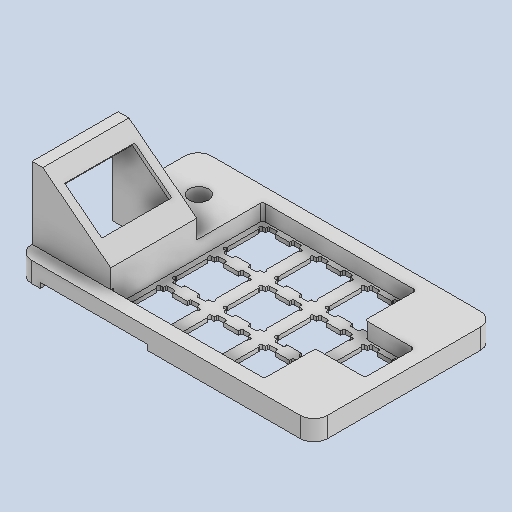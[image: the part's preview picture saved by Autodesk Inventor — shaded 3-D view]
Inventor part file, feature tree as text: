
AUTODESK INVENTOR PART (.ipt)
format: ipt  version: 2025.2 (Build 292293000, 293)  size: 1,165,312 bytes
history: native  units: mm
features: sketch x11, extrude x10, plane x2, fillet x2
ambient origin geometry x8: Origin, YZ Plane, XZ Plane, XY Plane, X Axis, Y Axis, Z Axis, Center Point
bodies: Solid1 (feature_tree)
feature tree (25):
  extrude  "Extrusion1"  Depth=19.0mm
  extrude  "Extrusion6"  Depth=1.5mm TaperAngle=0.0deg
  plane  "Work Plane3"
  sketch  "Sketch6"  dims[d41=2.0mm d43=6.0mm d44=0.0mm]
  extrude  "Extrusion7"  Depth=2.0mm
  extrude  "Extrusion8"  Depth=6.0mm TaperAngle=0.0deg
  sketch  "Sketch9"  dims[d51=32.0mm d52=7.0mm d53=0.0mm d54=32.0mm d55=4.0mm]
  plane  "Work Plane4"
  extrude  "Extrusion9"  Depth=31.0mm
  sketch  "Sketch10"  dims[d56=6.615149mm d57=7.0mm d58=0.0mm]
  extrude  "Extrusion10"  Depth=5.0mm
  extrude  "Extrusion11"  Depth=7.0mm TaperAngle=0.0deg
  fillet  "Fillet1"  Radius=32.0mm
  fillet  "Fillet2"  Radius=4.0mm
  extrude  "Extrusion12"  Depth=7.0mm TaperAngle=0.0deg
  extrude  "Extrusion13"  Depth=2.0mm
  extrude  "Extrusion14"  [1 undecoded]
  sketch  "Sketch1"  dims[d0=14.5mm d1=14.5mm d2=3.5mm d3=1.2mm d4=1.0mm d5=1.2mm d6=0.1mm d7=0.1mm d8=0.5mm d9=0.25mm d13=40.0mm d15=19.0mm d16=30.0mm d18=19.0mm d21=115.0mm]
  sketch  "Sketch Rectangular Pattern1"  dims[d22=75.0mm d23=1.5mm d24=0.0mm]
  sketch  "Sketch4"  dims[d38=2.0mm d40=2.0mm]
  sketch  "Sketch7"  dims[d47=225.0deg d48=31.0mm]
  sketch  "Sketch8"  dims[d49=30.0mm d50=5.0mm]
  sketch  "Sketch11"  dims[d60=1.5mm d61=2.0mm]
  sketch  "Sketch12"  dims[d62=2.0mm d63=-2.0mm]
  sketch  "Sketch13"  dims[d64=28.0mm d65=0.0mm d66=29.304175mm d67=28.0mm d68=23.0mm d69=23.0mm d70=1.5mm d71=1.5mm d72=0.75mm d73=17.5mm d74=26.0mm d75=0.0mm d76=0.0mm d77=5.0mm d78=0.0mm d79=2.0mm d80=2.0mm d81=29.25mm d82=4.0mm d83=7.27mm d84=1.0mm d85=5.0mm d86=7.25mm d87=0.0mm d88=0.0mm d89=15.0mm d90=15.0mm d91=3.0mm d92=8.25mm d93=40.0mm d94=2.0mm d95=0.0mm d96=4.0mm d97=4.0mm d98=4.0mm d99=5.0mm d100=0.0mm]
note: 1 required parameter value undecoded (feature->parameter linkage not recoverable at this tier; creation-order binding heuristic only, values carry confidence <= 0.55)
